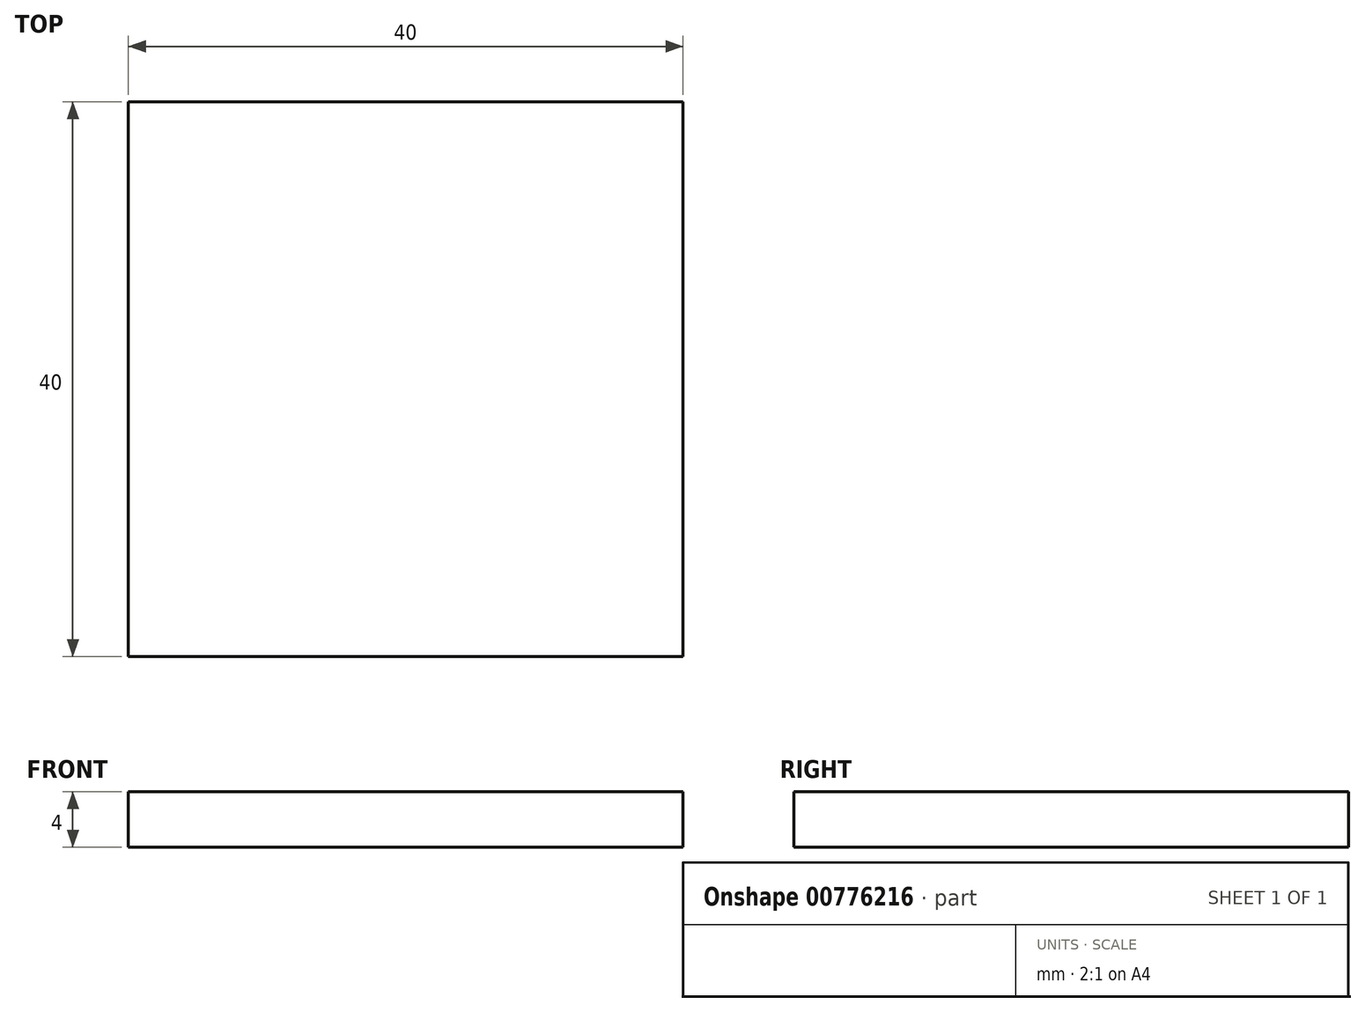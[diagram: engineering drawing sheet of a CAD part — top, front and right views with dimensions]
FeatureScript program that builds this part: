
annotation { "Feature Type Name" : "Feature", "Feature Type Description" : "" }
export const myFeature = defineFeature(function(context is Context, id is Id, definition is map)
    precondition{}
    {
        {
            var Q0;
            Q0=qCreatedBy(makeId("Top.planeOp"),FACE);
            var sketch = newSketch(context, id + "F0", { "sketchPlane" : qUnion([Q0])});
            skLineSegment(sketch, "E0.bottom", {"start": v(-20, 20) * mm, "end": v(20, 20) * mm});
            skLineSegment(sketch, "E0.top", {"start": v(-20, -20) * mm, "end": v(20, -20) * mm});
            skLineSegment(sketch, "E0.left", {"start": v(-20, 20) * mm, "end": v(-20, -20) * mm});
            skLineSegment(sketch, "E0.right", {"start": v(20, 20) * mm, "end": v(20, -20) * mm});
            skPoint(sketch, "E0.middle", {"position": v(0, 0) * mm});
            skSolve(sketch);
        }
        {
            var Q0;
            Q0=qSketchRegion(id+"F0",true);
            extrude(context, id + "F1", {"entities" : qUnion([Q0]), "depth" : 4 * mm, "offsetDistance" : 25 * mm});
        }
    });
